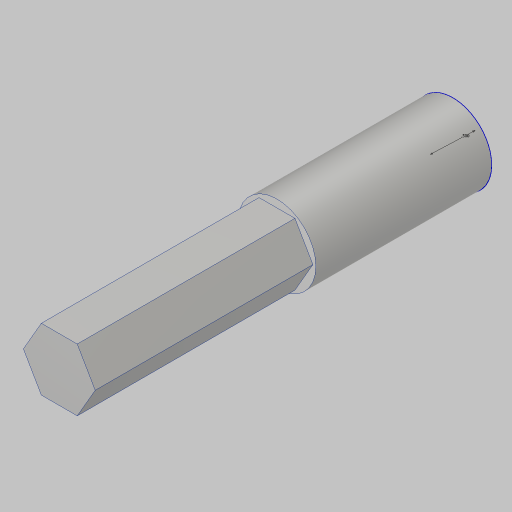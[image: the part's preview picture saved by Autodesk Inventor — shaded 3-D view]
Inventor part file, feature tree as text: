
AUTODESK INVENTOR PART (.ipt)
format: ipt  version: 2023.5 (Build 275446000, 446)  size: 139,776 bytes
history: native  units: in
note: dims shown in document units (in); Inventor stores cm internally (conversion verified against a paired STEP export)
features: sketch x5, extrude x4, projected_geometry x3
ambient origin geometry x8: Origin, YZ Plane, XZ Plane, XY Plane, X Axis, Y Axis, Z Axis, Center Point
bodies: Solid1 (feature_tree)
feature tree (12):
  extrude  "Extrusion1"  Depth=3.5625in TaperAngle=0.0deg
  extrude  "Extrusion2"  Depth=0.5in TaperAngle=0.0deg
  extrude  "Extrusion3"  Depth=0.5in TaperAngle=0.0deg
  extrude  "Extrusion6"  Depth=0.025in
  sketch  "Sketch7"  dims[d17=1.0in d18=0.0in d19=0.5in]
  sketch  "Sketch1"  dims[d0=0.625in d1=3.5625in d2=0.0in]
  sketch  "Sketch2"  dims[d3=0.5in d4=2.125in d5=0.0in]
  projected_geometry  "Projected Loop1"
  sketch  "Sketch3"  dims[d6=0.5in d7=0.25in d8=0.0in]
  projected_geometry  "Projected Loop2"
  sketch  "Sketch6"  dims[d15=0.375in d16=0.025in]
  projected_geometry  "Project Cut Edges3"
